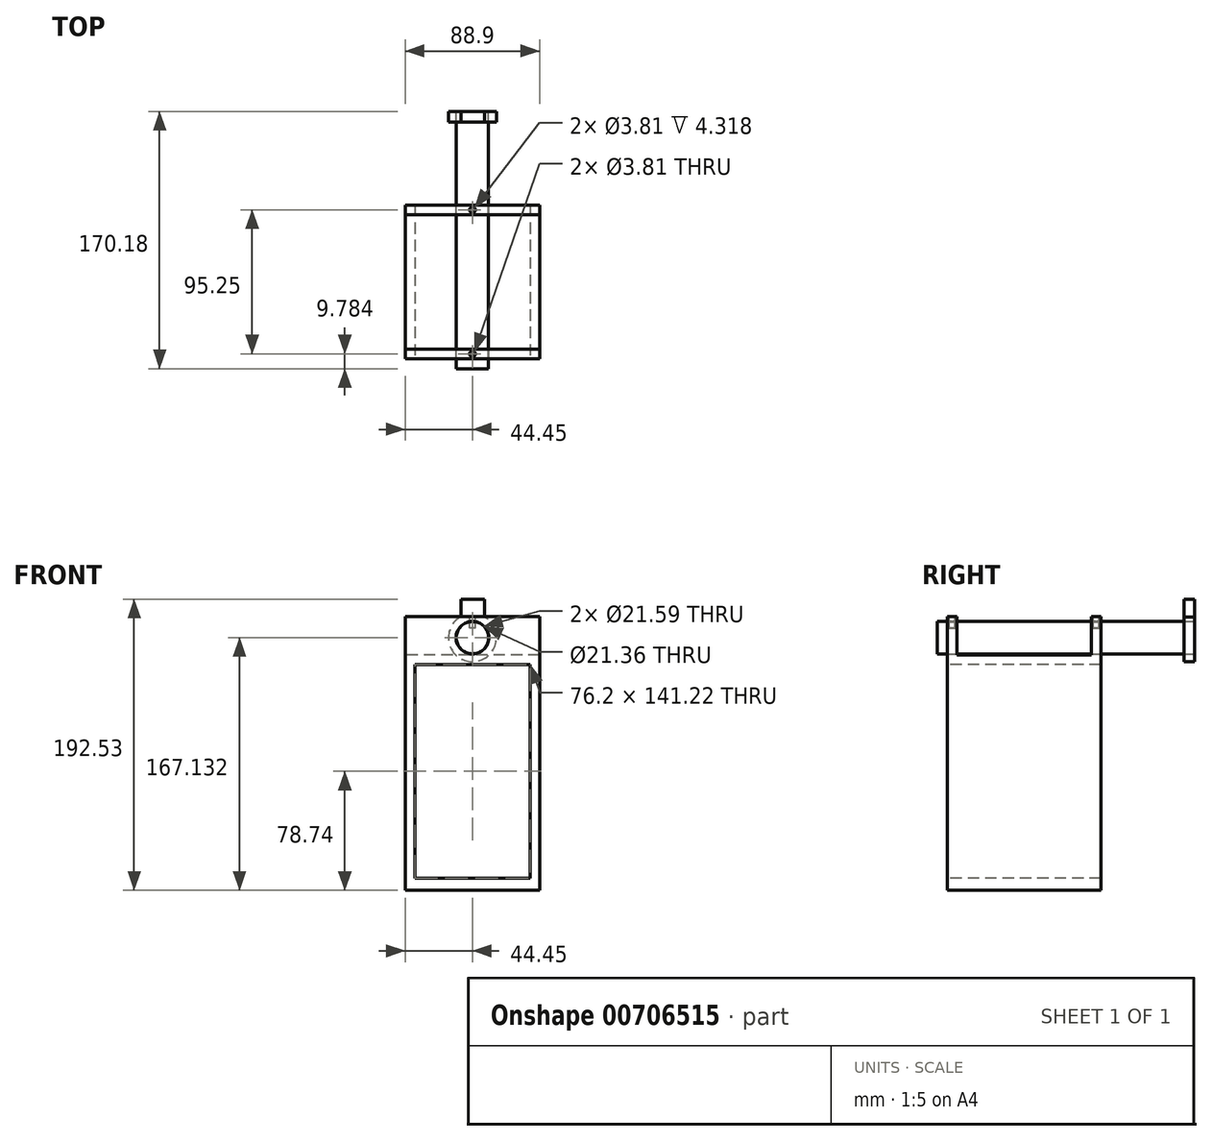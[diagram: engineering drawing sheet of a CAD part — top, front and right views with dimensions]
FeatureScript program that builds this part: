
annotation { "Feature Type Name" : "Feature", "Feature Type Description" : "" }
export const myFeature = defineFeature(function(context is Context, id is Id, definition is map)
    precondition{}
    {
        {
            var Q0;
            Q0=qCreatedBy(makeId("Top.planeOp"),FACE);
            var sketch = newSketch(context, id + "F0", { "sketchPlane" : qUnion([Q0])});
            skLineSegment(sketch, "E0.bottom", {"start": v(-36.85, 89.56) * mm, "end": v(52.05, 89.56) * mm});
            skLineSegment(sketch, "E0.top", {"start": v(-36.85, -12.04) * mm, "end": v(52.05, -12.04) * mm});
            skLineSegment(sketch, "E0.left", {"start": v(-36.85, 89.56) * mm, "end": v(-36.85, -12.04) * mm});
            skLineSegment(sketch, "E0.right", {"start": v(52.05, 89.56) * mm, "end": v(52.05, -12.04) * mm});
            skSolve(sketch);
        }
        {
            var Q0;
            Q0=makeQuery(id+"F0.imprint","IMPRINT",FACE,{"disambiguationData":[TD([[makeQuery(id+"F0.imprint","IMPRINT",EDGE,{"derivedFrom":sQuery(id+"F0.wireOp",EDGE,"E0.bottom")}),-1.0]])]});
            extrude(context, id + "F1", {"entities" : qUnion([Q0]), "depth" : 8.13 * mm, "offsetDistance" : 25.4 * mm});
        }
        {
            var Q0;
            Q0=makeQuery(id+"F1.opExtrude","CAP_FACE",FACE,{"disambiguationData":[OSD([sQuery(id+"F0.wireOp",EDGE,"E0.bottom"),sQuery(id+"F0.wireOp",EDGE,"E0.top"),sQuery(id+"F0.wireOp",EDGE,"E0.left"),sQuery(id+"F0.wireOp",EDGE,"E0.right")])],"isStart":false});
            var sketch = newSketch(context, id + "F2", { "sketchPlane" : qUnion([Q0])});
            skLineSegment(sketch, "E1.bottom", {"start": v(-36.85, 89.56) * mm, "end": v(-30.5, 89.56) * mm});
            skLineSegment(sketch, "E1.top", {"start": v(-36.85, -12.04) * mm, "end": v(-30.5, -12.04) * mm});
            skLineSegment(sketch, "E1.left", {"start": v(-36.85, 89.56) * mm, "end": v(-36.85, -12.04) * mm});
            skLineSegment(sketch, "E1.right", {"start": v(-30.5, 89.56) * mm, "end": v(-30.5, -12.04) * mm});
            skLineSegment(sketch, "E2.bottom", {"start": v(52.05, 89.56) * mm, "end": v(45.7, 89.56) * mm});
            skLineSegment(sketch, "E2.top", {"start": v(52.05, -12.04) * mm, "end": v(45.7, -12.04) * mm});
            skLineSegment(sketch, "E2.left", {"start": v(52.05, 89.56) * mm, "end": v(52.05, -12.04) * mm});
            skLineSegment(sketch, "E2.right", {"start": v(45.7, 89.56) * mm, "end": v(45.7, -12.04) * mm});
            skSolve(sketch);
        }
        {
            var Q0;
            Q0=makeQuery(id+"F2.imprint","IMPRINT",FACE,{"disambiguationData":[TD([[makeQuery(id+"F2.imprint","IMPRINT",EDGE,{"derivedFrom":sQuery(id+"F2.wireOp",EDGE,"E2.bottom")}),-1.0]])]});
            var Q1;
            Q1=makeQuery(id+"F2.imprint","IMPRINT",FACE,{"disambiguationData":[TD([[makeQuery(id+"F2.imprint","IMPRINT",EDGE,{"derivedFrom":sQuery(id+"F2.wireOp",EDGE,"E1.bottom")}),-1.0]])]});
            extrude(context, id + "F3", {"entities" : qUnion([Q0, Q1]), "operationType" : NewBodyOperationType.ADD, "depth" : 141.22 * mm, "offsetDistance" : 25.4 * mm});
        }
        {
            var Q0;
            Q0=makeQuery(id+"F3.boolean.opBoolean","MERGE",FACE,{"derivedFrom":[makeQuery(id+"F1.opExtrude","SWEPT_FACE",FACE,{"disambiguationData":[OSD([sQuery(id+"F0.wireOp",EDGE,"E0.bottom")])]}),makeQuery(id+"F3.opExtrude","SWEPT_FACE",FACE,{"disambiguationData":[OSD([sQuery(id+"F2.wireOp",EDGE,"E1.bottom")])]}),makeQuery(id+"F3.opExtrude","SWEPT_FACE",FACE,{"disambiguationData":[OSD([sQuery(id+"F2.wireOp",EDGE,"E2.bottom")])]})]});
            var sketch = newSketch(context, id + "F4", { "sketchPlane" : qUnion([Q0])});
            skLineSegment(sketch, "E3.bottom", {"start": v(-52.05, 149.35) * mm, "end": v(36.85, 149.35) * mm});
            skLineSegment(sketch, "E3.top", {"start": v(-52.05, 155.7) * mm, "end": v(36.85, 155.7) * mm});
            skLineSegment(sketch, "E3.left", {"start": v(-52.05, 149.35) * mm, "end": v(-52.05, 155.7) * mm});
            skLineSegment(sketch, "E3.right", {"start": v(36.85, 149.35) * mm, "end": v(36.85, 155.7) * mm});
            skSolve(sketch);
        }
        {
            var Q0;
            Q0=makeQuery(id+"F4.imprint","IMPRINT",FACE,{"disambiguationData":[TD([[makeQuery(id+"F4.imprint","IMPRINT",EDGE,{"derivedFrom":sQuery(id+"F4.wireOp",EDGE,"E3.top")}),-1.0]])]});
            extrude(context, id + "F5", {"entities" : qUnion([Q0]), "operationType" : NewBodyOperationType.ADD, "oppositeDirection" : true, "depth" : 101.6 * mm, "offsetDistance" : 25.4 * mm});
        }
        {
            var Q0;
            Q0=makeQuery(id+"F5.opExtrude","SWEPT_FACE",FACE,{"disambiguationData":[OSD([sQuery(id+"F4.wireOp",EDGE,"E3.top")])]});
            var sketch = newSketch(context, id + "F6", { "sketchPlane" : qUnion([Q0])});
            skLineSegment(sketch, "E4.bottom", {"start": v(52.05, 89.56) * mm, "end": v(-36.85, 89.56) * mm});
            skLineSegment(sketch, "E4.top", {"start": v(52.05, 83.2) * mm, "end": v(-36.85, 83.2) * mm});
            skLineSegment(sketch, "E4.left", {"start": v(52.05, 89.56) * mm, "end": v(52.05, 83.2) * mm});
            skLineSegment(sketch, "E4.right", {"start": v(-36.85, 89.56) * mm, "end": v(-36.85, 83.2) * mm});
            skLineSegment(sketch, "E5.bottom", {"start": v(52.05, -5.7) * mm, "end": v(-36.85, -5.7) * mm});
            skLineSegment(sketch, "E5.top", {"start": v(52.05, -12.04) * mm, "end": v(-36.85, -12.04) * mm});
            skLineSegment(sketch, "E5.left", {"start": v(52.05, -5.7) * mm, "end": v(52.05, -12.04) * mm});
            skLineSegment(sketch, "E5.right", {"start": v(-36.85, -5.7) * mm, "end": v(-36.85, -12.04) * mm});
            skSolve(sketch);
        }
        {
            var Q0;
            Q0=makeQuery(id+"F6.imprint","IMPRINT",FACE,{"disambiguationData":[TD([[makeQuery(id+"F6.imprint","IMPRINT",EDGE,{"derivedFrom":sQuery(id+"F6.wireOp",EDGE,"E5.bottom")}),1.0]])]});
            var Q1;
            Q1=makeQuery(id+"F6.imprint","IMPRINT",FACE,{"disambiguationData":[TD([[makeQuery(id+"F6.imprint","IMPRINT",EDGE,{"derivedFrom":sQuery(id+"F6.wireOp",EDGE,"E4.bottom")}),1.0]])]});
            extrude(context, id + "F7", {"entities" : qUnion([Q0, Q1]), "operationType" : NewBodyOperationType.ADD, "depth" : 25.4 * mm, "offsetDistance" : 25.4 * mm});
        }
        {
            var Q0;
            Q0=makeQuery(id+"F7.boolean.opBoolean","MERGE",FACE,{"derivedFrom":[makeQuery(id+"F5.boolean.opBoolean","MERGE",FACE,{"derivedFrom":[makeQuery(id+"F3.boolean.opBoolean","MERGE",FACE,{"derivedFrom":[makeQuery(id+"F1.opExtrude","SWEPT_FACE",FACE,{"disambiguationData":[OSD([sQuery(id+"F0.wireOp",EDGE,"E0.bottom")])]}),makeQuery(id+"F3.opExtrude","SWEPT_FACE",FACE,{"disambiguationData":[OSD([sQuery(id+"F2.wireOp",EDGE,"E1.bottom")])]}),makeQuery(id+"F3.opExtrude","SWEPT_FACE",FACE,{"disambiguationData":[OSD([sQuery(id+"F2.wireOp",EDGE,"E2.bottom")])]})]}),makeQuery(id+"F5.opExtrude","CAP_FACE",FACE,{"disambiguationData":[OSD([sQuery(id+"F4.wireOp",EDGE,"E3.bottom"),sQuery(id+"F4.wireOp",EDGE,"E3.top"),sQuery(id+"F4.wireOp",EDGE,"E3.left"),sQuery(id+"F4.wireOp",EDGE,"E3.right")])],"isStart":true})]}),makeQuery(id+"F7.opExtrude","SWEPT_FACE",FACE,{"disambiguationData":[OSD([sQuery(id+"F6.wireOp",EDGE,"E4.bottom")])]})]});
            var sketch = newSketch(context, id + "F8", { "sketchPlane" : qUnion([Q0])});
            skCircle(sketch, "E6", {"center": v(-7.6, 167.13) * mm, "radius": 10.8 * mm});
            skLineSegment(sketch, "E7", {"start": v(-7.6, 167.13) * mm, "end": v(-52.05, 167.13) * mm});
            skLineSegment(sketch, "E8", {"start": v(-7.6, 167.13) * mm, "end": v(36.85, 167.13) * mm});
            skSolve(sketch);
        }
        {
            var Q0;
            {var subQ0=sQuery(id+"F8.wireOp",EDGE,"E7");var subQ1=sQuery(id+"F8.wireOp",EDGE,"E6");var subQ2=makeQuery(id+"F8.imprint","INTERSECT",VERTEX,{"derivedFrom":[subQ1,subQ0]});Q0=makeQuery(id+"F8.imprint","IMPRINT",FACE,{"disambiguationData":[TD([[makeQuery(id+"F8.imprint","IMPRINT",EDGE,{"disambiguationData":[TD([[subQ2,1.0]])],"derivedFrom":subQ1}),1.0]])]});}
            var Q1;
            {var subQ0=sQuery(id+"F8.wireOp",EDGE,"E7");var subQ1=sQuery(id+"F8.wireOp",EDGE,"E6");var subQ2=makeQuery(id+"F8.imprint","INTERSECT",VERTEX,{"derivedFrom":[subQ1,subQ0]});Q1=makeQuery(id+"F8.imprint","IMPRINT",FACE,{"disambiguationData":[TD([[makeQuery(id+"F8.imprint","IMPRINT",EDGE,{"disambiguationData":[TD([[subQ2,-1.0]])],"derivedFrom":subQ1}),1.0]])]});}
            extrude(context, id + "F9", {"entities" : qUnion([Q0, Q1]), "operationType" : NewBodyOperationType.REMOVE, "oppositeDirection" : true, "depth" : 153.16 * mm, "offsetDistance" : 25.4 * mm});
        }
        {
            var Q0;
            Q0=makeQuery(id+"F7.boolean.opBoolean","MERGE",FACE,{"derivedFrom":[makeQuery(id+"F5.boolean.opBoolean","MERGE",FACE,{"derivedFrom":[makeQuery(id+"F3.boolean.opBoolean","MERGE",FACE,{"derivedFrom":[makeQuery(id+"F1.opExtrude","SWEPT_FACE",FACE,{"disambiguationData":[OSD([sQuery(id+"F0.wireOp",EDGE,"E0.bottom")])]}),makeQuery(id+"F3.opExtrude","SWEPT_FACE",FACE,{"disambiguationData":[OSD([sQuery(id+"F2.wireOp",EDGE,"E1.bottom")])]}),makeQuery(id+"F3.opExtrude","SWEPT_FACE",FACE,{"disambiguationData":[OSD([sQuery(id+"F2.wireOp",EDGE,"E2.bottom")])]})]}),makeQuery(id+"F5.opExtrude","CAP_FACE",FACE,{"disambiguationData":[OSD([sQuery(id+"F4.wireOp",EDGE,"E3.bottom"),sQuery(id+"F4.wireOp",EDGE,"E3.top"),sQuery(id+"F4.wireOp",EDGE,"E3.left"),sQuery(id+"F4.wireOp",EDGE,"E3.right")])],"isStart":true})]}),makeQuery(id+"F7.opExtrude","SWEPT_FACE",FACE,{"disambiguationData":[OSD([sQuery(id+"F6.wireOp",EDGE,"E4.bottom")])]})]});
            var sketch = newSketch(context, id + "F10", { "sketchPlane" : qUnion([Q0])});
            skCircle(sketch, "E9", {"center": v(-7.6, 167.13) * mm, "radius": 10.67 * mm});
            skSolve(sketch);
        }
        {
            var Q0;
            Q0=makeQuery(id+"F10.imprint","IMPRINT",FACE,{"disambiguationData":[TD([[makeQuery(id+"F10.imprint","IMPRINT",EDGE,{"derivedFrom":sQuery(id+"F10.wireOp",EDGE,"E9")}),1.0]])]});
            extrude(context, id + "F11", {"entities" : qUnion([Q0]), "oppositeDirection" : true, "depth" : 108.2 * mm, "offsetDistance" : 25.4 * mm});
        }
        {
            var Q0;
            Q0=makeQuery(id+"F11.opExtrude","CAP_FACE",FACE,{"disambiguationData":[OSD([sQuery(id+"F10.wireOp",EDGE,"E9")])],"isStart":true});
            extrude(context, id + "F12", {"entities" : qUnion([Q0]), "operationType" : NewBodyOperationType.ADD, "depth" : 61.98 * mm, "offsetDistance" : 25.4 * mm});
        }
        {
            var Q0;
            Q0=makeQuery(id+"F12.opExtrude","CAP_FACE",FACE,{"disambiguationData":[OSD([sQuery(id+"F10.wireOp",EDGE,"E9")])],"isStart":false});
            var sketch = newSketch(context, id + "F13", { "sketchPlane" : qUnion([Q0])});
            skCircle(sketch, "E10", {"center": v(-7.6, 167.13) * mm, "radius": 15.88 * mm});
            skLineSegment(sketch, "E11", {"start": v(-7.6, 167.13) * mm, "end": v(-23.48, 167.13) * mm});
            skLineSegment(sketch, "E12", {"start": v(-7.6, 167.13) * mm, "end": v(8.27, 167.13) * mm});
            skLineSegment(sketch, "E13", {"start": v(-7.6, 167.13) * mm, "end": v(-7.6, 183) * mm});
            skLineSegment(sketch, "E14.bottom", {"start": v(-15.54, 167.13) * mm, "end": v(0, 167.13) * mm});
            skLineSegment(sketch, "E14.top", {"start": v(-15.54, 192.53) * mm, "end": v(0, 192.53) * mm});
            skLineSegment(sketch, "E14.left", {"start": v(-15.54, 167.13) * mm, "end": v(-15.54, 192.53) * mm});
            skLineSegment(sketch, "E14.right", {"start": v(0, 167.13) * mm, "end": v(0, 192.53) * mm});
            skCircle(sketch, "E15", {"center": v(-7.6, 167.13) * mm, "radius": 10.68 * mm});
            skSolve(sketch);
        }
        {
            var Q0;
            {var subQ0=sQuery(id+"F13.wireOp",EDGE,"E11");var subQ1=sQuery(id+"F13.wireOp",EDGE,"E10");var subQ2=makeQuery(id+"F13.imprint","INTERSECT",VERTEX,{"derivedFrom":[subQ1,subQ0]});Q0=makeQuery(id+"F13.imprint","IMPRINT",FACE,{"disambiguationData":[TD([[makeQuery(id+"F13.imprint","IMPRINT",EDGE,{"disambiguationData":[TD([[subQ2,-1.0]])],"derivedFrom":subQ1}),1.0]])]});}
            var Q1;
            {var subQ0=sQuery(id+"F13.wireOp",EDGE,"E11");var subQ1=sQuery(id+"F13.wireOp",EDGE,"E10");var subQ2=makeQuery(id+"F13.imprint","INTERSECT",VERTEX,{"derivedFrom":[subQ1,subQ0]});Q1=makeQuery(id+"F13.imprint","IMPRINT",FACE,{"disambiguationData":[TD([[makeQuery(id+"F13.imprint","IMPRINT",EDGE,{"disambiguationData":[TD([[subQ2,1.0]])],"derivedFrom":subQ1}),1.0]])]});}
            var Q2;
            {var subQ0=sQuery(id+"F13.wireOp",EDGE,"E13");var subQ1=sQuery(id+"F13.wireOp",EDGE,"E10");var subQ2=makeQuery(id+"F13.imprint","INTERSECT",VERTEX,{"derivedFrom":[subQ1,subQ0]});Q2=makeQuery(id+"F13.imprint","IMPRINT",FACE,{"disambiguationData":[TD([[makeQuery(id+"F13.imprint","IMPRINT",EDGE,{"disambiguationData":[TD([[subQ2,1.0]])],"derivedFrom":subQ1}),1.0]])]});}
            var Q3;
            {var subQ0=sQuery(id+"F13.wireOp",EDGE,"E12");var subQ1=sQuery(id+"F13.wireOp",EDGE,"E10");var subQ2=makeQuery(id+"F13.imprint","INTERSECT",VERTEX,{"derivedFrom":[subQ1,subQ0]});Q3=makeQuery(id+"F13.imprint","IMPRINT",FACE,{"disambiguationData":[TD([[makeQuery(id+"F13.imprint","IMPRINT",EDGE,{"disambiguationData":[TD([[subQ2,-1.0]])],"derivedFrom":subQ1}),1.0]])]});}
            var Q4;
            {var subQ0=sQuery(id+"F13.wireOp",EDGE,"E13");var subQ1=sQuery(id+"F13.wireOp",EDGE,"E10");var subQ2=makeQuery(id+"F13.imprint","INTERSECT",VERTEX,{"derivedFrom":[subQ1,subQ0]});Q4=makeQuery(id+"F13.imprint","IMPRINT",FACE,{"disambiguationData":[TD([[makeQuery(id+"F13.imprint","IMPRINT",EDGE,{"disambiguationData":[TD([[subQ2,-1.0]])],"derivedFrom":subQ1}),1.0]])]});}
            var Q5;
            {var subQ0=sQuery(id+"F13.wireOp",EDGE,"E14.top");Q5=makeQuery(id+"F13.imprint","IMPRINT",FACE,{"disambiguationData":[TD([[makeQuery(id+"F13.imprint","IMPRINT",EDGE,{"derivedFrom":subQ0}),-1.0]])]});}
            extrude(context, id + "F14", {"entities" : qUnion([Q0, Q1, Q2, Q3, Q4, Q5]), "operationType" : NewBodyOperationType.ADD, "depth" : -7 * mm, "offsetDistance" : 25.4 * mm});
        }
        {
            var Q0;
            Q0=makeQuery(id+"F7.opExtrude","CAP_FACE",FACE,{"disambiguationData":[OSD([sQuery(id+"F6.wireOp",EDGE,"E5.bottom"),sQuery(id+"F6.wireOp",EDGE,"E5.top"),sQuery(id+"F6.wireOp",EDGE,"E5.left"),sQuery(id+"F6.wireOp",EDGE,"E5.right")])],"isStart":false});
            var sketch = newSketch(context, id + "F15", { "sketchPlane" : qUnion([Q0])});
            skLineSegment(sketch, "E16", {"start": v(52.05, -5.7) * mm, "end": v(-36.85, -5.7) * mm});
            skLineSegment(sketch, "E17", {"start": v(7.6, -5.7) * mm, "end": v(7.6, -12.04) * mm});
            skCircle(sketch, "E18", {"center": v(7.6, -8.87) * mm, "radius": 1.9 * mm});
            skSolve(sketch);
        }
        {
            var Q0;
            {var subQ0=sQuery(id+"F15.wireOp",EDGE,"E18");var subQ1=sQuery(id+"F15.wireOp",EDGE,"E17");var subQ2=makeQuery(id+"F15.imprint","INTERSECT",VERTEX,{"disambiguationData":[OD(0.0)],"derivedFrom":[subQ1,subQ0]});Q0=makeQuery(id+"F15.imprint","IMPRINT",FACE,{"disambiguationData":[TD([[makeQuery(id+"F15.imprint","IMPRINT",EDGE,{"disambiguationData":[TD([[subQ2,-1.0]])],"derivedFrom":subQ1}),1.0]])]});}
            var Q1;
            {var subQ0=sQuery(id+"F15.wireOp",EDGE,"E18");var subQ1=sQuery(id+"F15.wireOp",EDGE,"E17");var subQ2=makeQuery(id+"F15.imprint","INTERSECT",VERTEX,{"disambiguationData":[OD(0.0)],"derivedFrom":[subQ1,subQ0]});Q1=makeQuery(id+"F15.imprint","IMPRINT",FACE,{"disambiguationData":[TD([[makeQuery(id+"F15.imprint","IMPRINT",EDGE,{"disambiguationData":[TD([[subQ2,-1.0]])],"derivedFrom":subQ1}),-1.0]])]});}
            extrude(context, id + "F16", {"entities" : qUnion([Q0, Q1]), "operationType" : NewBodyOperationType.REMOVE, "oppositeDirection" : true, "depth" : 7.62 * mm, "offsetDistance" : 25.4 * mm});
        }
        {
            var Q0;
            Q0=makeQuery(id+"F7.opExtrude","CAP_FACE",FACE,{"disambiguationData":[OSD([sQuery(id+"F6.wireOp",EDGE,"E4.bottom"),sQuery(id+"F6.wireOp",EDGE,"E4.top"),sQuery(id+"F6.wireOp",EDGE,"E4.left"),sQuery(id+"F6.wireOp",EDGE,"E4.right")])],"isStart":false});
            var sketch = newSketch(context, id + "F17", { "sketchPlane" : qUnion([Q0])});
            skLineSegment(sketch, "E19", {"start": v(52.05, 89.56) * mm, "end": v(-36.85, 89.56) * mm});
            skLineSegment(sketch, "E20", {"start": v(7.6, 89.56) * mm, "end": v(7.6, 83.2) * mm});
            skCircle(sketch, "E21", {"center": v(7.6, 86.38) * mm, "radius": 1.9 * mm});
            skSolve(sketch);
        }
        {
            var Q0;
            {var subQ0=sQuery(id+"F17.wireOp",EDGE,"E21");var subQ1=sQuery(id+"F17.wireOp",EDGE,"E20");var subQ2=makeQuery(id+"F17.imprint","INTERSECT",VERTEX,{"disambiguationData":[OD(0.0)],"derivedFrom":[subQ1,subQ0]});Q0=makeQuery(id+"F17.imprint","IMPRINT",FACE,{"disambiguationData":[TD([[makeQuery(id+"F17.imprint","IMPRINT",EDGE,{"disambiguationData":[TD([[subQ2,-1.0]])],"derivedFrom":subQ1}),1.0]])]});}
            var Q1;
            {var subQ0=sQuery(id+"F17.wireOp",EDGE,"E21");var subQ1=sQuery(id+"F17.wireOp",EDGE,"E20");var subQ2=makeQuery(id+"F17.imprint","INTERSECT",VERTEX,{"disambiguationData":[OD(0.0)],"derivedFrom":[subQ1,subQ0]});Q1=makeQuery(id+"F17.imprint","IMPRINT",FACE,{"disambiguationData":[TD([[makeQuery(id+"F17.imprint","IMPRINT",EDGE,{"disambiguationData":[TD([[subQ2,-1.0]])],"derivedFrom":subQ1}),-1.0]])]});}
            extrude(context, id + "F18", {"entities" : qUnion([Q0, Q1]), "operationType" : NewBodyOperationType.REMOVE, "oppositeDirection" : true, "depth" : 7.62 * mm, "offsetDistance" : 25.4 * mm});
        }
    });
